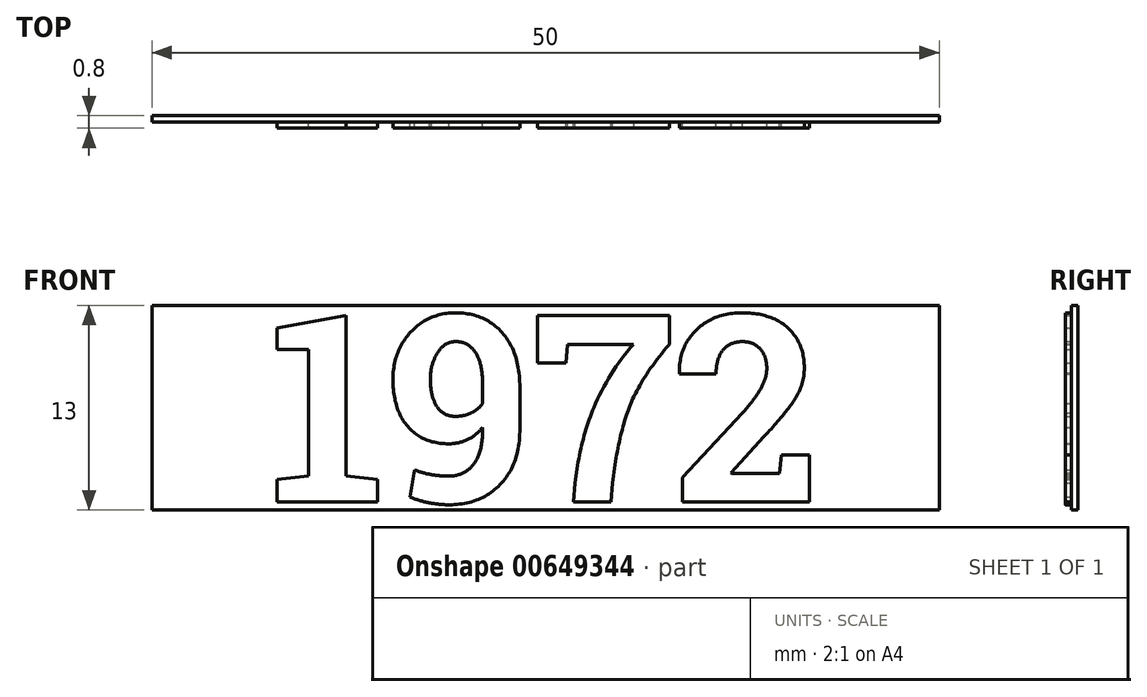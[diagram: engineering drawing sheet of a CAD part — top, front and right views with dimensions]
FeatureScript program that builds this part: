
annotation { "Feature Type Name" : "Feature", "Feature Type Description" : "" }
export const myFeature = defineFeature(function(context is Context, id is Id, definition is map)
    precondition{}
    {
        {
            var Q0;
            Q0=qCreatedBy(makeId("Front.planeOp"),FACE);
            var sketch = newSketch(context, id + "F0", { "sketchPlane" : qUnion([Q0])});
            skLineSegment(sketch, "E0.bottom", {"start": v(25, 6.5) * mm, "end": v(-25, 6.5) * mm});
            skLineSegment(sketch, "E0.top", {"start": v(25, -6.5) * mm, "end": v(-25, -6.5) * mm});
            skLineSegment(sketch, "E0.left", {"start": v(25, 6.5) * mm, "end": v(25, -6.5) * mm});
            skLineSegment(sketch, "E0.right", {"start": v(-25, 6.5) * mm, "end": v(-25, -6.5) * mm});
            skPoint(sketch, "E0.middle", {"position": v(0, 0) * mm});
            skSolve(sketch);
        }
        {
            var Q0;
            Q0 = qSketchRegion(id + "F0", true);
            extrude(context, id + "F1", {"entities" : qUnion([Q0]), "depth" : .4 * mm, "offsetDistance" : 25 * mm});
        }
        {
            var Q0;
            Q0=makeQuery(id+"F1.opExtrude","CAP_FACE",FACE,{"disambiguationData":[OSD([sQuery(id+"F0.wireOp",EDGE,"E0.bottom"),sQuery(id+"F0.wireOp",EDGE,"E0.top"),sQuery(id+"F0.wireOp",EDGE,"E0.left"),sQuery(id+"F0.wireOp",EDGE,"E0.right")])],"isStart":false});
            var sketch = newSketch(context, id + "F2", { "sketchPlane" : qUnion([Q0])});
            skText(sketch, "E1", { "text": "1972", "fontName": "RobotoSlab-Bold.ttf"});
            const initialGuessF2  = {"E1": [-0.01757, -0.006, 1, 0, 0.012]};
            skSetInitialGuess(sketch, initialGuessF2);
            skSolve(sketch);
        }
        {
            var Q0;
            Q0 = qSketchRegion(id + "F2", true);
            extrude(context, id + "F3", {"entities" : qUnion([Q0]), "operationType" : NewBodyOperationType.ADD, "depth" : .4 * mm, "offsetDistance" : 25 * mm});
        }
    });
